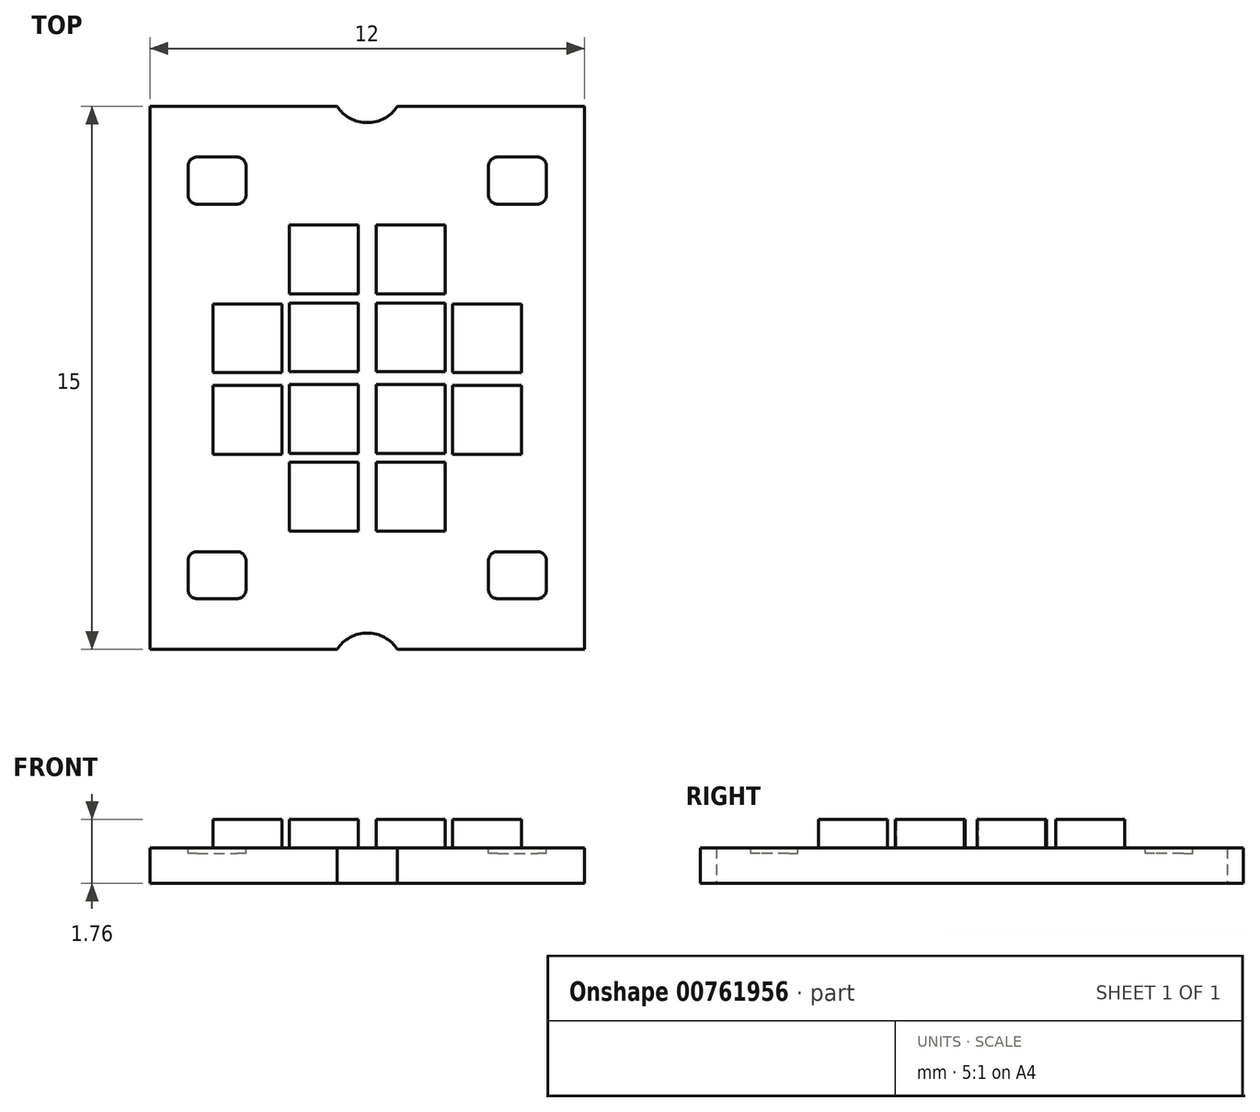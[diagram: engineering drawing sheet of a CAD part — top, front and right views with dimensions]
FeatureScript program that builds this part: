
annotation { "Feature Type Name" : "Feature", "Feature Type Description" : "" }
export const myFeature = defineFeature(function(context is Context, id is Id, definition is map)
    precondition{}
    {
        {
            var Q0;
            Q0=qCreatedBy(makeId("Top.planeOp"),FACE);
            var sketch = newSketch(context, id + "F0", { "sketchPlane" : qUnion([Q0])});
            skLineSegment(sketch, "E0.bottom", {"start": v(6, -7.5) * mm, "end": v(-6, -7.5) * mm});
            skLineSegment(sketch, "E0.top", {"start": v(6, 7.5) * mm, "end": v(-6, 7.5) * mm});
            skLineSegment(sketch, "E0.left", {"start": v(6, -7.5) * mm, "end": v(6, 7.5) * mm});
            skLineSegment(sketch, "E0.right", {"start": v(-6, -7.5) * mm, "end": v(-6, 7.5) * mm});
            skPoint(sketch, "E0.middle", {"position": v(0, 0) * mm});
            skLineSegment(sketch, "E1", {"start": v(0, 7.5) * mm, "end": v(0, 8.05) * mm});
            skCircle(sketch, "E2", {"center": v(0, 8.05) * mm, "radius": 1 * mm});
            skLineSegment(sketch, "E3", {"start": v(0, 0) * mm, "end": v(1.67, 0) * mm});
            skCircle(sketch, "E4.MirrorC", {"center": v(0, -8.05) * mm, "radius": 1 * mm});
            skSolve(sketch);
        }
        {
            var Q0;
            {var subQ4=sQuery(id+"F0.wireOp",EDGE,"E0.left");Q0=makeQuery(id+"F0.imprint","IMPRINT",FACE,{"disambiguationData":[TD([[makeQuery(id+"F0.imprint","IMPRINT",EDGE,{"derivedFrom":subQ4}),1.0]])]});}
            extrude(context, id + "F1", {"entities" : qUnion([Q0]), "depth" : .98 * mm, "offsetDistance" : 25 * mm});
        }
        {
            var Q0;
            Q0=makeQuery(id+"F1.opExtrude","CAP_FACE",FACE,{"disambiguationData":[OSD([sQuery(id+"F0.wireOp",EDGE,"E0.bottom"),sQuery(id+"F0.wireOp",EDGE,"E0.top"),sQuery(id+"F0.wireOp",EDGE,"E0.left"),sQuery(id+"F0.wireOp",EDGE,"E0.right"),sQuery(id+"F0.wireOp",EDGE,"E2"),sQuery(id+"F0.wireOp",EDGE,"E4.MirrorC")])],"isStart":false});
            var sketch = newSketch(context, id + "F2", { "sketchPlane" : qUnion([Q0])});
            skLineSegment(sketch, "E5", {"start": v(-6, 7.5) * mm, "end": v(-6, 6.1) * mm});
            skLineSegment(sketch, "E6", {"start": v(-4.7, 6.1) * mm, "end": v(-3.6, 6.1) * mm});
            skLineSegment(sketch, "E7", {"start": v(-3.35, 5.85) * mm, "end": v(-3.35, 5.05) * mm});
            skLineSegment(sketch, "E8", {"start": v(-3.6, 4.8) * mm, "end": v(-4.7, 4.8) * mm});
            skLineSegment(sketch, "E9", {"start": v(-4.95, 5.05) * mm, "end": v(-4.95, 5.85) * mm});
            skPoint(sketch, "E10.visualSharp", {"position": v(-3.35, 4.8) * mm});
            skArc(sketch, "E10.filletArc", {"start": v(-3.6, 4.8) * mm, "mid": v(-3.42, 4.87) * mm, "end": v(-3.35, 5.05) * mm});
            skPoint(sketch, "E11.visualSharp", {"position": v(-3.35, 6.1) * mm});
            skArc(sketch, "E11.filletArc", {"start": v(-3.35, 5.85) * mm, "mid": v(-3.42, 6.03) * mm, "end": v(-3.6, 6.1) * mm});
            skPoint(sketch, "E12.visualSharp", {"position": v(-4.95, 6.1) * mm});
            skArc(sketch, "E12.filletArc", {"start": v(-4.7, 6.1) * mm, "mid": v(-4.88, 6.03) * mm, "end": v(-4.95, 5.85) * mm});
            skPoint(sketch, "E13.visualSharp", {"position": v(-4.95, 4.8) * mm});
            skArc(sketch, "E13.filletArc", {"start": v(-4.95, 5.05) * mm, "mid": v(-4.88, 4.87) * mm, "end": v(-4.7, 4.8) * mm});
            skLineSegment(sketch, "E14", {"start": v(0, 0) * mm, "end": v(0, 0.84) * mm});
            skLineSegment(sketch, "E15", {"start": v(0, 0.84) * mm, "end": v(0, 0) * mm});
            skLineSegment(sketch, "E16", {"start": v(-1.02, 0) * mm, "end": v(0, 0) * mm});
            skArc(sketch, "E17.MirrorCS", {"start": v(-4.7, -6.1) * mm, "mid": v(-4.88, -6.03) * mm, "end": v(-4.95, -5.85) * mm});
            skArc(sketch, "E18.MirrorCS", {"start": v(-3.6, -4.8) * mm, "mid": v(-3.42, -4.87) * mm, "end": v(-3.35, -5.05) * mm});
            skArc(sketch, "E19.MirrorCS", {"start": v(-3.35, -5.85) * mm, "mid": v(-3.42, -6.03) * mm, "end": v(-3.6, -6.1) * mm});
            skArc(sketch, "E20.MirrorCS", {"start": v(-4.95, -5.05) * mm, "mid": v(-4.88, -4.87) * mm, "end": v(-4.7, -4.8) * mm});
            skLineSegment(sketch, "E21.MirrorCS", {"start": v(-4.95, -5.05) * mm, "end": v(-4.95, -5.85) * mm});
            skLineSegment(sketch, "E22.MirrorCS", {"start": v(-3.6, -4.8) * mm, "end": v(-4.7, -4.8) * mm});
            skLineSegment(sketch, "E23.MirrorCS", {"start": v(-3.35, -5.85) * mm, "end": v(-3.35, -5.05) * mm});
            skLineSegment(sketch, "E24.MirrorCS", {"start": v(-4.7, -6.1) * mm, "end": v(-3.6, -6.1) * mm});
            skPoint(sketch, "E25.MirrorP", {"position": v(-4.95, -4.8) * mm});
            skPoint(sketch, "E26.MirrorP", {"position": v(-3.35, -4.8) * mm});
            skPoint(sketch, "E27.MirrorP", {"position": v(-4.95, -6.1) * mm});
            skPoint(sketch, "E28.MirrorP", {"position": v(-3.35, -6.1) * mm});
            skArc(sketch, "E29.MirrorCS", {"start": v(3.6, 4.8) * mm, "mid": v(3.42, 4.87) * mm, "end": v(3.35, 5.05) * mm});
            skLineSegment(sketch, "E30.MirrorCS", {"start": v(4.95, 5.05) * mm, "end": v(4.95, 5.85) * mm});
            skArc(sketch, "E31.MirrorCS", {"start": v(3.35, 5.85) * mm, "mid": v(3.42, 6.03) * mm, "end": v(3.6, 6.1) * mm});
            skArc(sketch, "E32.MirrorCS", {"start": v(4.7, 6.1) * mm, "mid": v(4.88, 6.03) * mm, "end": v(4.95, 5.85) * mm});
            skArc(sketch, "E33.MirrorCS", {"start": v(4.95, 5.05) * mm, "mid": v(4.88, 4.87) * mm, "end": v(4.7, 4.8) * mm});
            skLineSegment(sketch, "E34.MirrorCS", {"start": v(3.35, 5.85) * mm, "end": v(3.35, 5.05) * mm});
            skArc(sketch, "E35.MirrorCS", {"start": v(3.35, -5.85) * mm, "mid": v(3.42, -6.03) * mm, "end": v(3.6, -6.1) * mm});
            skArc(sketch, "E36.MirrorCS", {"start": v(3.6, -4.8) * mm, "mid": v(3.42, -4.87) * mm, "end": v(3.35, -5.05) * mm});
            skArc(sketch, "E37.MirrorCS", {"start": v(4.7, -6.1) * mm, "mid": v(4.88, -6.03) * mm, "end": v(4.95, -5.85) * mm});
            skLineSegment(sketch, "E38.MirrorCS", {"start": v(4.95, -5.05) * mm, "end": v(4.95, -5.85) * mm});
            skLineSegment(sketch, "E39.MirrorCS", {"start": v(3.35, -5.85) * mm, "end": v(3.35, -5.05) * mm});
            skArc(sketch, "E40.MirrorCS", {"start": v(4.95, -5.05) * mm, "mid": v(4.88, -4.87) * mm, "end": v(4.7, -4.8) * mm});
            skLineSegment(sketch, "E41.MirrorCS", {"start": v(3.6, 4.8) * mm, "end": v(4.7, 4.8) * mm});
            skLineSegment(sketch, "E42.MirrorCS", {"start": v(4.7, 6.1) * mm, "end": v(3.6, 6.1) * mm});
            skPoint(sketch, "E43.MirrorP", {"position": v(4.95, 6.1) * mm});
            skPoint(sketch, "E44.MirrorP", {"position": v(4.95, -4.8) * mm});
            skPoint(sketch, "E45.MirrorP", {"position": v(4.95, -6.1) * mm});
            skPoint(sketch, "E46.MirrorP", {"position": v(3.35, 4.8) * mm});
            skPoint(sketch, "E47.MirrorP", {"position": v(3.35, 6.1) * mm});
            skLineSegment(sketch, "E48.MirrorCS", {"start": v(3.6, -4.8) * mm, "end": v(4.7, -4.8) * mm});
            skPoint(sketch, "E49.MirrorP", {"position": v(3.35, -6.1) * mm});
            skLineSegment(sketch, "E50.MirrorCS", {"start": v(4.7, -6.1) * mm, "end": v(3.6, -6.1) * mm});
            skPoint(sketch, "E51.MirrorP", {"position": v(3.35, -4.8) * mm});
            skPoint(sketch, "E52.MirrorP", {"position": v(4.95, 4.8) * mm});
            skSolve(sketch);
        }
        {
            var Q0;
            Q0 = qSketchRegion(id + "F2", true);
            extrude(context, id + "F3", {"entities" : qUnion([Q0]), "operationType" : NewBodyOperationType.REMOVE, "oppositeDirection" : true, "depth" : .16 * mm, "offsetDistance" : 25 * mm});
        }
        {
            var Q0;
            Q0=makeQuery(id+"F1.opExtrude","CAP_FACE",FACE,{"disambiguationData":[OSD([sQuery(id+"F0.wireOp",EDGE,"E0.bottom"),sQuery(id+"F0.wireOp",EDGE,"E0.top"),sQuery(id+"F0.wireOp",EDGE,"E0.left"),sQuery(id+"F0.wireOp",EDGE,"E0.right"),sQuery(id+"F0.wireOp",EDGE,"E2"),sQuery(id+"F0.wireOp",EDGE,"E4.MirrorC")])],"isStart":false});
            var sketch = newSketch(context, id + "F4", { "sketchPlane" : qUnion([Q0])});
            skCircle(sketch, "E53", {"center": v(0, 0) * mm, "radius": 4.75 * mm});
            skLineSegment(sketch, "E54", {"start": v(0, 0) * mm, "end": v(0, 5.42) * mm});
            skLineSegment(sketch, "E55", {"start": v(0, 0) * mm, "end": v(7.49, 0) * mm});
            skLineSegment(sketch, "E56.bottom", {"start": v(0.25, 0.17) * mm, "end": v(2.15, 0.17) * mm});
            skLineSegment(sketch, "E56.top", {"start": v(0.25, 2.07) * mm, "end": v(2.15, 2.07) * mm});
            skLineSegment(sketch, "E56.left", {"start": v(0.25, 0.17) * mm, "end": v(0.25, 2.07) * mm});
            skLineSegment(sketch, "E56.right", {"start": v(2.15, 0.17) * mm, "end": v(2.15, 2.07) * mm});
            skPoint(sketch, "E56.middle", {"position": v(1.2, 1.12) * mm});
            skLineSegment(sketch, "E57.bottom", {"start": v(0.25, 2.32) * mm, "end": v(2.15, 2.32) * mm});
            skLineSegment(sketch, "E57.top", {"start": v(0.25, 4.22) * mm, "end": v(2.15, 4.22) * mm});
            skLineSegment(sketch, "E57.left", {"start": v(0.25, 2.32) * mm, "end": v(0.25, 4.22) * mm});
            skLineSegment(sketch, "E57.right", {"start": v(2.15, 2.32) * mm, "end": v(2.15, 4.22) * mm});
            skPoint(sketch, "E57.middle", {"position": v(1.2, 3.27) * mm});
            skLineSegment(sketch, "E58.MirrorCS", {"start": v(-0.25, 0.17) * mm, "end": v(-0.25, 2.07) * mm});
            skLineSegment(sketch, "E59.MirrorCS", {"start": v(-2.15, 0.17) * mm, "end": v(-2.15, 2.07) * mm});
            skLineSegment(sketch, "E60.MirrorCS", {"start": v(-2.15, 2.32) * mm, "end": v(-2.15, 4.22) * mm});
            skLineSegment(sketch, "E61.MirrorCS", {"start": v(-0.25, 2.32) * mm, "end": v(-2.15, 2.32) * mm});
            skPoint(sketch, "E62.MirrorP", {"position": v(-1.2, 3.27) * mm});
            skLineSegment(sketch, "E63.MirrorCS", {"start": v(-0.25, 2.07) * mm, "end": v(-2.15, 2.07) * mm});
            skLineSegment(sketch, "E64.MirrorCS", {"start": v(-0.25, 0.17) * mm, "end": v(-2.15, 0.17) * mm});
            skPoint(sketch, "E65.MirrorP", {"position": v(-1.2, 1.12) * mm});
            skLineSegment(sketch, "E66.MirrorCS", {"start": v(-0.25, 4.22) * mm, "end": v(-2.15, 4.22) * mm});
            skLineSegment(sketch, "E67.MirrorCS", {"start": v(-0.25, 2.32) * mm, "end": v(-0.25, 4.22) * mm});
            skPoint(sketch, "E68.MirrorP", {"position": v(1.2, -3.29) * mm});
            skLineSegment(sketch, "E69.MirrorCS", {"start": v(-0.25, -4.24) * mm, "end": v(-2.15, -4.24) * mm});
            skPoint(sketch, "E70.MirrorP", {"position": v(-1.2, -1.14) * mm});
            skLineSegment(sketch, "E71.MirrorCS", {"start": v(-2.15, -0.19) * mm, "end": v(-2.15, -2.09) * mm});
            skLineSegment(sketch, "E72.MirrorCS", {"start": v(-0.25, -0.19) * mm, "end": v(-0.25, -2.09) * mm});
            skLineSegment(sketch, "E73.MirrorCS", {"start": v(2.15, -2.34) * mm, "end": v(2.15, -4.24) * mm});
            skLineSegment(sketch, "E74.MirrorCS", {"start": v(0.25, -2.34) * mm, "end": v(0.25, -4.24) * mm});
            skLineSegment(sketch, "E75.MirrorCS", {"start": v(-0.25, -2.09) * mm, "end": v(-2.15, -2.09) * mm});
            skPoint(sketch, "E76.MirrorP", {"position": v(-1.2, -3.29) * mm});
            skLineSegment(sketch, "E77.MirrorCS", {"start": v(-0.25, -0.19) * mm, "end": v(-2.15, -0.19) * mm});
            skLineSegment(sketch, "E78.MirrorCS", {"start": v(-0.25, -2.34) * mm, "end": v(-2.15, -2.34) * mm});
            skPoint(sketch, "E79.MirrorP", {"position": v(1.2, -1.14) * mm});
            skLineSegment(sketch, "E80.MirrorCS", {"start": v(0.25, -4.24) * mm, "end": v(2.15, -4.24) * mm});
            skLineSegment(sketch, "E81.MirrorCS", {"start": v(-0.25, -2.34) * mm, "end": v(-0.25, -4.24) * mm});
            skLineSegment(sketch, "E82.MirrorCS", {"start": v(0.25, -0.19) * mm, "end": v(2.15, -0.19) * mm});
            skLineSegment(sketch, "E83.MirrorCS", {"start": v(0.25, -2.09) * mm, "end": v(2.15, -2.09) * mm});
            skLineSegment(sketch, "E84.MirrorCS", {"start": v(0.25, -2.34) * mm, "end": v(2.15, -2.34) * mm});
            skLineSegment(sketch, "E85.MirrorCS", {"start": v(0.25, -0.19) * mm, "end": v(0.25, -2.09) * mm});
            skLineSegment(sketch, "E86.MirrorCS", {"start": v(-2.15, -2.34) * mm, "end": v(-2.15, -4.24) * mm});
            skLineSegment(sketch, "E87.MirrorCS", {"start": v(2.15, -0.19) * mm, "end": v(2.15, -2.09) * mm});
            skPoint(sketch, "E88.MirrorP", {"position": v(-0.12, -1.11) * mm});
            skPoint(sketch, "E89.MirrorP", {"position": v(-0.12, -3.37) * mm});
            skLineSegment(sketch, "E90.MirrorCS", {"start": v(-2.36, 0.14) * mm, "end": v(-2.36, 2.04) * mm});
            skLineSegment(sketch, "E91.MirrorCS", {"start": v(-4.26, 0.14) * mm, "end": v(-4.26, 2.04) * mm});
            skLineSegment(sketch, "E92.MirrorCS", {"start": v(-2.36, 2.04) * mm, "end": v(-4.26, 2.04) * mm});
            skLineSegment(sketch, "E93.MirrorCS", {"start": v(-2.36, 0.14) * mm, "end": v(-4.26, 0.14) * mm});
            skPoint(sketch, "E94.MirrorP", {"position": v(-3.3, 1.1) * mm});
            skPoint(sketch, "E95.MirrorP", {"position": v(-3.3, -1.16) * mm});
            skLineSegment(sketch, "E96.MirrorCS", {"start": v(-4.26, -0.21) * mm, "end": v(-4.26, -2.11) * mm});
            skLineSegment(sketch, "E97.MirrorCS", {"start": v(-2.36, -0.21) * mm, "end": v(-2.36, -2.11) * mm});
            skLineSegment(sketch, "E98.MirrorCS", {"start": v(-2.36, -2.11) * mm, "end": v(-4.26, -2.11) * mm});
            skLineSegment(sketch, "E99.MirrorCS", {"start": v(-2.36, -0.21) * mm, "end": v(-4.26, -0.21) * mm});
            skLineSegment(sketch, "E100.MirrorCS", {"start": v(4.26, -0.21) * mm, "end": v(4.26, -2.11) * mm});
            skLineSegment(sketch, "E101.MirrorCS", {"start": v(2.36, -0.21) * mm, "end": v(2.36, -2.11) * mm});
            skPoint(sketch, "E102.MirrorP", {"position": v(3.3, -1.16) * mm});
            skPoint(sketch, "E103.MirrorP", {"position": v(3.3, 1.1) * mm});
            skLineSegment(sketch, "E104.MirrorCS", {"start": v(2.36, 0.14) * mm, "end": v(4.26, 0.14) * mm});
            skLineSegment(sketch, "E105.MirrorCS", {"start": v(2.36, -2.11) * mm, "end": v(4.26, -2.11) * mm});
            skLineSegment(sketch, "E106.MirrorCS", {"start": v(2.36, -0.21) * mm, "end": v(4.26, -0.21) * mm});
            skLineSegment(sketch, "E107.MirrorCS", {"start": v(2.36, 2.04) * mm, "end": v(4.26, 2.04) * mm});
            skLineSegment(sketch, "E108.MirrorCS", {"start": v(4.26, 0.14) * mm, "end": v(4.26, 2.04) * mm});
            skLineSegment(sketch, "E109.MirrorCS", {"start": v(2.36, 0.14) * mm, "end": v(2.36, 2.04) * mm});
            skSolve(sketch);
        }
        {
            var Q0;
            Q0=makeQuery(id+"F4.imprint","IMPRINT",FACE,{"disambiguationData":[TD([[makeQuery(id+"F4.imprint","IMPRINT",EDGE,{"derivedFrom":sQuery(id+"F4.wireOp",EDGE,"E60.MirrorCS")}),-1.0]])]});
            var Q1;
            Q1=makeQuery(id+"F4.imprint","IMPRINT",FACE,{"disambiguationData":[TD([[makeQuery(id+"F4.imprint","IMPRINT",EDGE,{"derivedFrom":sQuery(id+"F4.wireOp",EDGE,"E57.bottom")}),1.0]])]});
            var Q2;
            Q2=makeQuery(id+"F4.imprint","IMPRINT",FACE,{"disambiguationData":[TD([[makeQuery(id+"F4.imprint","IMPRINT",EDGE,{"derivedFrom":sQuery(id+"F4.wireOp",EDGE,"E56.bottom")}),1.0]])]});
            var Q3;
            Q3=makeQuery(id+"F4.imprint","IMPRINT",FACE,{"disambiguationData":[TD([[makeQuery(id+"F4.imprint","IMPRINT",EDGE,{"derivedFrom":sQuery(id+"F4.wireOp",EDGE,"E104.MirrorCS")}),1.0]])]});
            var Q4;
            Q4=makeQuery(id+"F4.imprint","IMPRINT",FACE,{"disambiguationData":[TD([[makeQuery(id+"F4.imprint","IMPRINT",EDGE,{"derivedFrom":sQuery(id+"F4.wireOp",EDGE,"E58.MirrorCS")}),1.0]])]});
            var Q5;
            Q5=makeQuery(id+"F4.imprint","IMPRINT",FACE,{"disambiguationData":[TD([[makeQuery(id+"F4.imprint","IMPRINT",EDGE,{"derivedFrom":sQuery(id+"F4.wireOp",EDGE,"E90.MirrorCS")}),1.0]])]});
            var Q6;
            Q6=makeQuery(id+"F4.imprint","IMPRINT",FACE,{"disambiguationData":[TD([[makeQuery(id+"F4.imprint","IMPRINT",EDGE,{"derivedFrom":sQuery(id+"F4.wireOp",EDGE,"E96.MirrorCS")}),1.0]])]});
            var Q7;
            Q7=makeQuery(id+"F4.imprint","IMPRINT",FACE,{"disambiguationData":[TD([[makeQuery(id+"F4.imprint","IMPRINT",EDGE,{"derivedFrom":sQuery(id+"F4.wireOp",EDGE,"E71.MirrorCS")}),1.0]])]});
            var Q8;
            Q8=makeQuery(id+"F4.imprint","IMPRINT",FACE,{"disambiguationData":[TD([[makeQuery(id+"F4.imprint","IMPRINT",EDGE,{"derivedFrom":sQuery(id+"F4.wireOp",EDGE,"E82.MirrorCS")}),-1.0]])]});
            var Q9;
            Q9=makeQuery(id+"F4.imprint","IMPRINT",FACE,{"disambiguationData":[TD([[makeQuery(id+"F4.imprint","IMPRINT",EDGE,{"derivedFrom":sQuery(id+"F4.wireOp",EDGE,"E100.MirrorCS")}),-1.0]])]});
            var Q10;
            Q10=makeQuery(id+"F4.imprint","IMPRINT",FACE,{"disambiguationData":[TD([[makeQuery(id+"F4.imprint","IMPRINT",EDGE,{"derivedFrom":sQuery(id+"F4.wireOp",EDGE,"E73.MirrorCS")}),-1.0]])]});
            var Q11;
            Q11=makeQuery(id+"F4.imprint","IMPRINT",FACE,{"disambiguationData":[TD([[makeQuery(id+"F4.imprint","IMPRINT",EDGE,{"derivedFrom":sQuery(id+"F4.wireOp",EDGE,"E69.MirrorCS")}),-1.0]])]});
            extrude(context, id + "F5", {"entities" : qUnion([Q0, Q1, Q2, Q3, Q4, Q5, Q6, Q7, Q8, Q9, Q10, Q11]), "operationType" : NewBodyOperationType.ADD, "depth" : .78 * mm, "offsetDistance" : 25 * mm});
        }
    });
